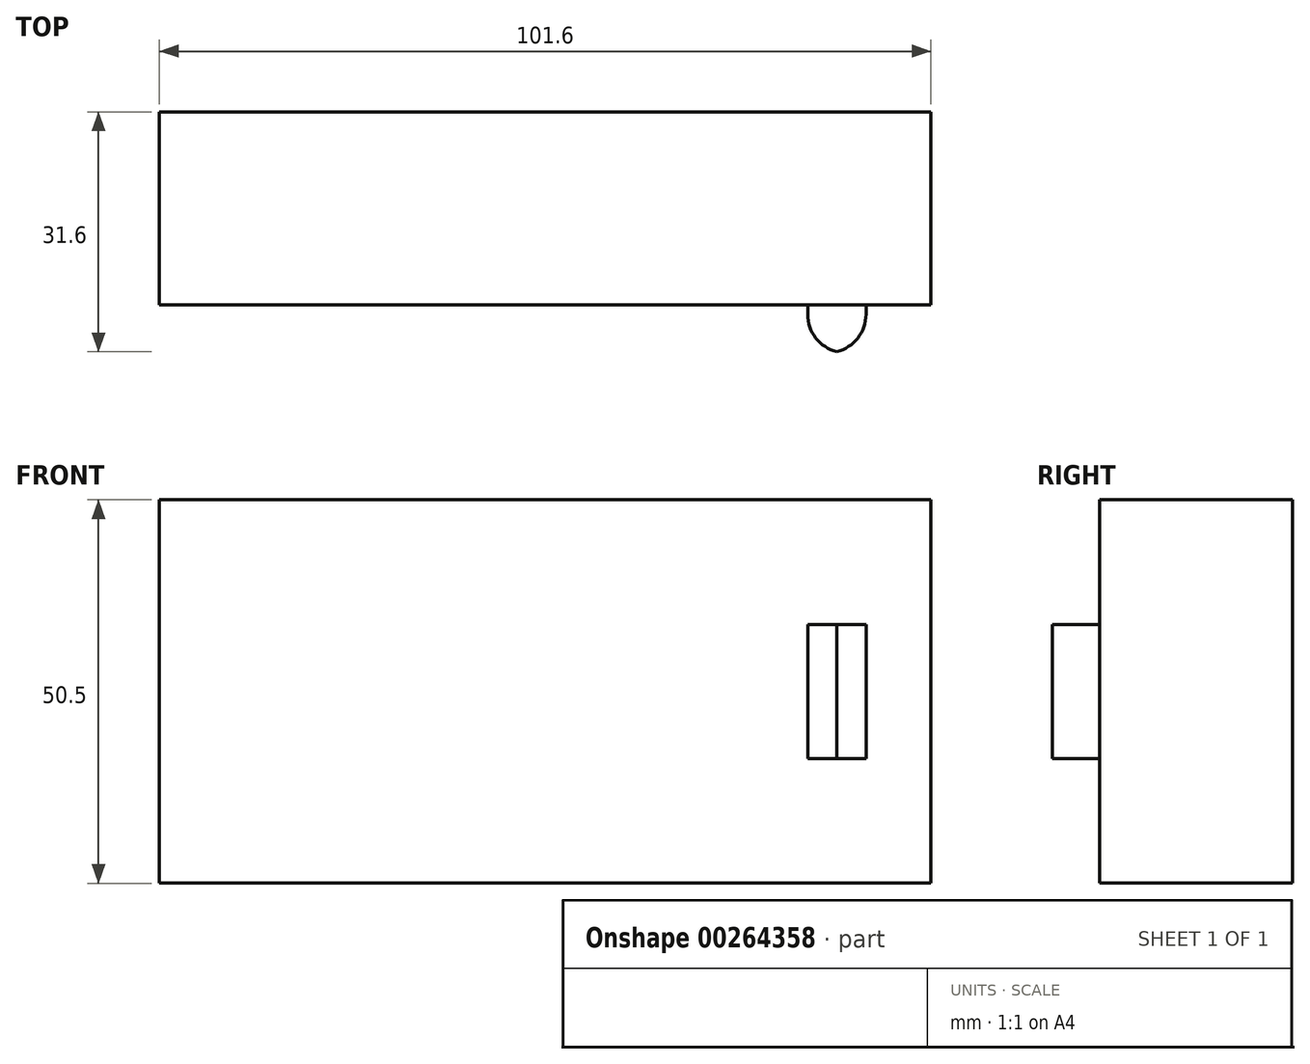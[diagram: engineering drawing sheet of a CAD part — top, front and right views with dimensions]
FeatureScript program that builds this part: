
annotation { "Feature Type Name" : "Feature", "Feature Type Description" : "" }
export const myFeature = defineFeature(function(context is Context, id is Id, definition is map)
    precondition{}
    {
        {
            var Q0;
            Q0=qCreatedBy(makeId("Front.planeOp"),FACE);
            var sketch = newSketch(context, id + "F0", { "sketchPlane" : qUnion([Q0])});
            skLineSegment(sketch, "E0.bottom", {"start": v(50.8, 25.25) * mm, "end": v(-50.8, 25.25) * mm});
            skLineSegment(sketch, "E0.top", {"start": v(50.8, -25.25) * mm, "end": v(-50.8, -25.25) * mm});
            skLineSegment(sketch, "E0.left", {"start": v(50.8, 25.25) * mm, "end": v(50.8, -25.25) * mm});
            skLineSegment(sketch, "E0.right", {"start": v(-50.8, 25.25) * mm, "end": v(-50.8, -25.25) * mm});
            skPoint(sketch, "E0.middle", {"position": v(0, 0) * mm});
            skLineSegment(sketch, "E1.bottom", {"start": v(42.25, 8.82) * mm, "end": v(34.57, 8.82) * mm});
            skLineSegment(sketch, "E1.top", {"start": v(42.25, -8.82) * mm, "end": v(34.57, -8.82) * mm});
            skLineSegment(sketch, "E1.left", {"start": v(42.25, 8.82) * mm, "end": v(42.25, -8.82) * mm});
            skLineSegment(sketch, "E1.right", {"start": v(34.57, 8.82) * mm, "end": v(34.57, -8.82) * mm});
            skPoint(sketch, "E1.middle", {"position": v(38.4, 0) * mm});
            skSolve(sketch);
        }
        {
            var Q0;
            Q0=makeQuery(id+"F0.imprint","IMPRINT",FACE,{"disambiguationData":[TD([[makeQuery(id+"F0.imprint","IMPRINT",EDGE,{"derivedFrom":sQuery(id+"F0.wireOp",EDGE,"E1.bottom")}),1.0]])]});
            extrude(context, id + "F1", {"entities" : qUnion([Q0]), "depth" : 31.75 * mm});
        }
        {
            var Q0;
            Q0=makeQuery(id+"F0.imprint","IMPRINT",FACE,{"disambiguationData":[TD([[makeQuery(id+"F0.imprint","IMPRINT",EDGE,{"derivedFrom":sQuery(id+"F0.wireOp",EDGE,"E0.bottom")}),1.0]])]});
            extrude(context, id + "F2", {"entities" : qUnion([Q0]), "operationType" : NewBodyOperationType.ADD, "depth" : 25.4 * mm});
        }
        {
            var Q0;
            Q0=makeQuery(id+"F1.opExtrude","CAP_EDGE",EDGE,{"disambiguationData":[OSD([sQuery(id+"F0.wireOp",EDGE,"E1.left")])],"isStart":false});
            var Q1;
            Q1=makeQuery(id+"F1.opExtrude","CAP_EDGE",EDGE,{"disambiguationData":[OSD([sQuery(id+"F0.wireOp",EDGE,"E1.right")])],"isStart":false});
            fillet(context, id + "F3", {"entities" : qUnion([Q0, Q1]), "radius" : 5.08 * mm, "tangentPropagation" : true, "allowEdgeOverflow" : false});
        }
    });
